# Revit family: Стол медицинский без тумбы эргономичный ДМ
name_source: partatom
category: Оборудование
revit_build: Autodesk Revit 2017 (Build: 20170118_1100(x64)
units: mm (PartAtom-declared; Revit-internal decimal feet)

## family parameters
Всегда вертикально = Да
На основе рабочей плоскости = Нет
Общий = Нет
При загрузке вырезать с полостями = Нет
Размер круглого соединителя = Использовать диаметр
Тип детали = Нормальный
Точка расчета площади = Нет

## types (2) — shared parameters
Длина ручек = 150 мм
Каркас = Алюминий 7075
Ножки = Пластмасса, непрозрачная, черная
Общ_Высота = 820 мм
Общ_Глубина = 1300 мм
Общ_Единицы измерения = шт.
Общ_Наименование = Стол медицинский без тумбы эргономичный правый
Общ_Поставщик = Доктор Мебель
Общ_Ширина = 1600 мм
Панели = Пластмасса, непрозрачная, белая
Ручки = Алюминий 7075
Фасад = Столешница медицинской мебели ДСП с пластиковым покрытием

## per-type parameters (varying)
| type | Общ_Тип, марка |
| Правый | ДМ-2-006-07 |
| Левый | ДМ-2-006-09 |
